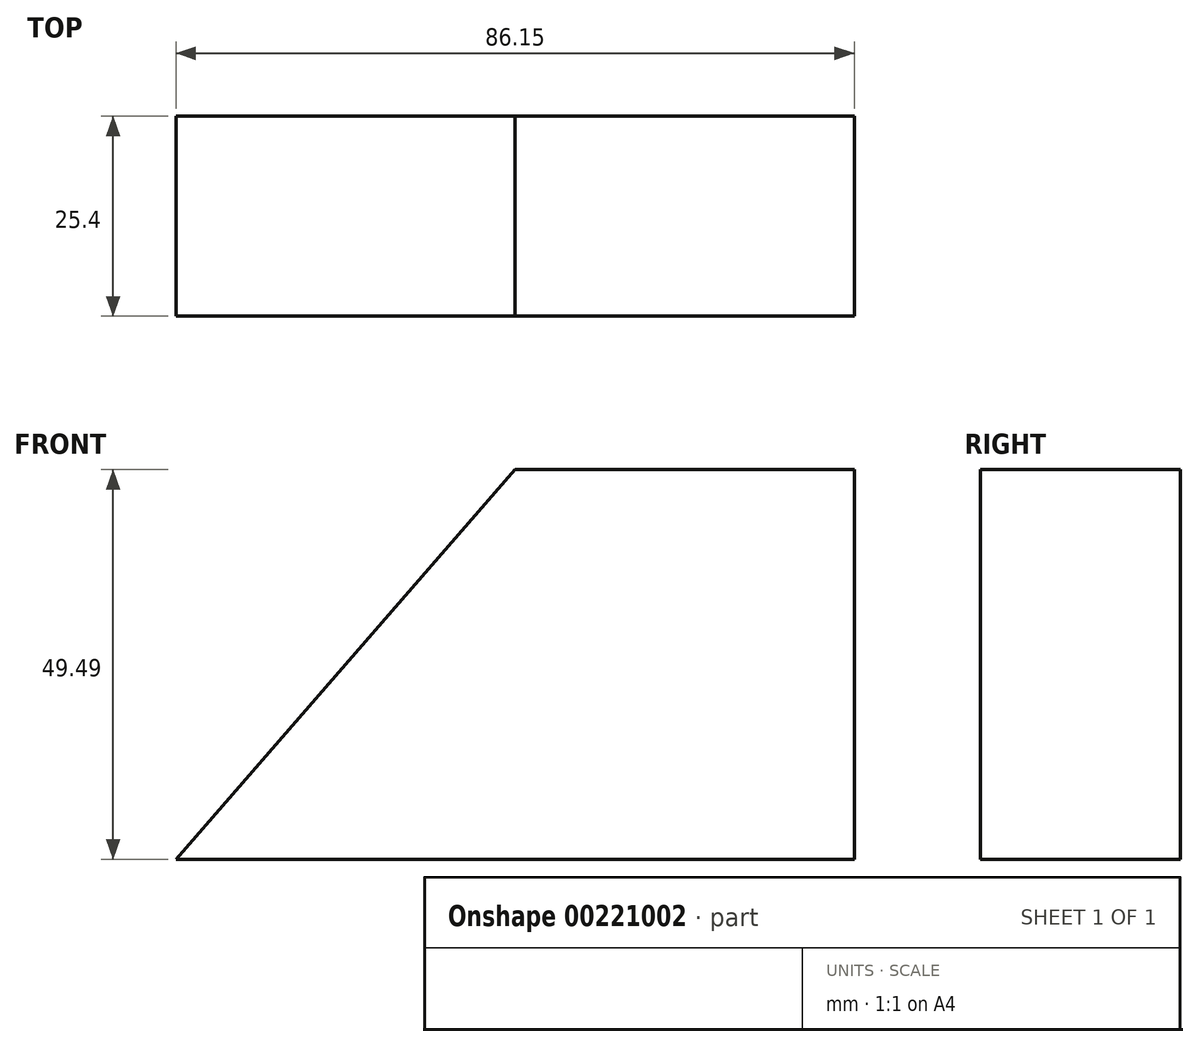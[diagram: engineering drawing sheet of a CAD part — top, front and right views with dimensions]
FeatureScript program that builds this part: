
annotation { "Feature Type Name" : "Feature", "Feature Type Description" : "" }
export const myFeature = defineFeature(function(context is Context, id is Id, definition is map)
    precondition{}
    {
        {
            var Q0;
            Q0=qCreatedBy(makeId("Front.planeOp"),FACE);
            var sketch = newSketch(context, id + "F0", { "sketchPlane" : qUnion([Q0])});
            skLineSegment(sketch, "E0.bottom", {"start": v(-45.64, 27.59) * mm, "end": v(40.5, 27.59) * mm});
            skLineSegment(sketch, "E0.top", {"start": v(-45.64, -21.9) * mm, "end": v(40.5, -21.9) * mm});
            skLineSegment(sketch, "E0.left", {"start": v(-45.64, 27.59) * mm, "end": v(-45.64, -21.9) * mm});
            skLineSegment(sketch, "E0.right", {"start": v(40.5, 27.59) * mm, "end": v(40.5, -21.9) * mm});
            skSolve(sketch);
        }
        {
            var Q0;
            Q0 = qSketchRegion(id + "F0", true);
            extrude(context, id + "F1", {"entities" : qUnion([Q0]), "depth" : 25.4 * mm});
        }
        {
            var Q0;
            Q0=makeQuery(id+"F1.opExtrude","CAP_FACE",FACE,{"disambiguationData":[OSD([sQuery(id+"F0.wireOp",EDGE,"E0.bottom"),sQuery(id+"F0.wireOp",EDGE,"E0.top"),sQuery(id+"F0.wireOp",EDGE,"E0.left"),sQuery(id+"F0.wireOp",EDGE,"E0.right")])],"isStart":false});
            var sketch = newSketch(context, id + "F2", { "sketchPlane" : qUnion([Q0])});
            skLineSegment(sketch, "E1", {"start": v(-45.64, -21.9) * mm, "end": v(-2.57, 27.59) * mm});
            skLineSegment(sketch, "E2", {"start": v(-45.64, -21.9) * mm, "end": v(-52.06, 31.44) * mm});
            skLineSegment(sketch, "E3", {"start": v(-52.06, 31.44) * mm, "end": v(-2.57, 27.59) * mm});
            skSolve(sketch);
        }
        {
            var Q0;
            Q0 = qSketchRegion(id + "F2", true);
            extrude(context, id + "F3", {"entities" : qUnion([Q0]), "operationType" : NewBodyOperationType.REMOVE, "oppositeDirection" : true, "depth" : 25.4 * mm});
        }
    });
